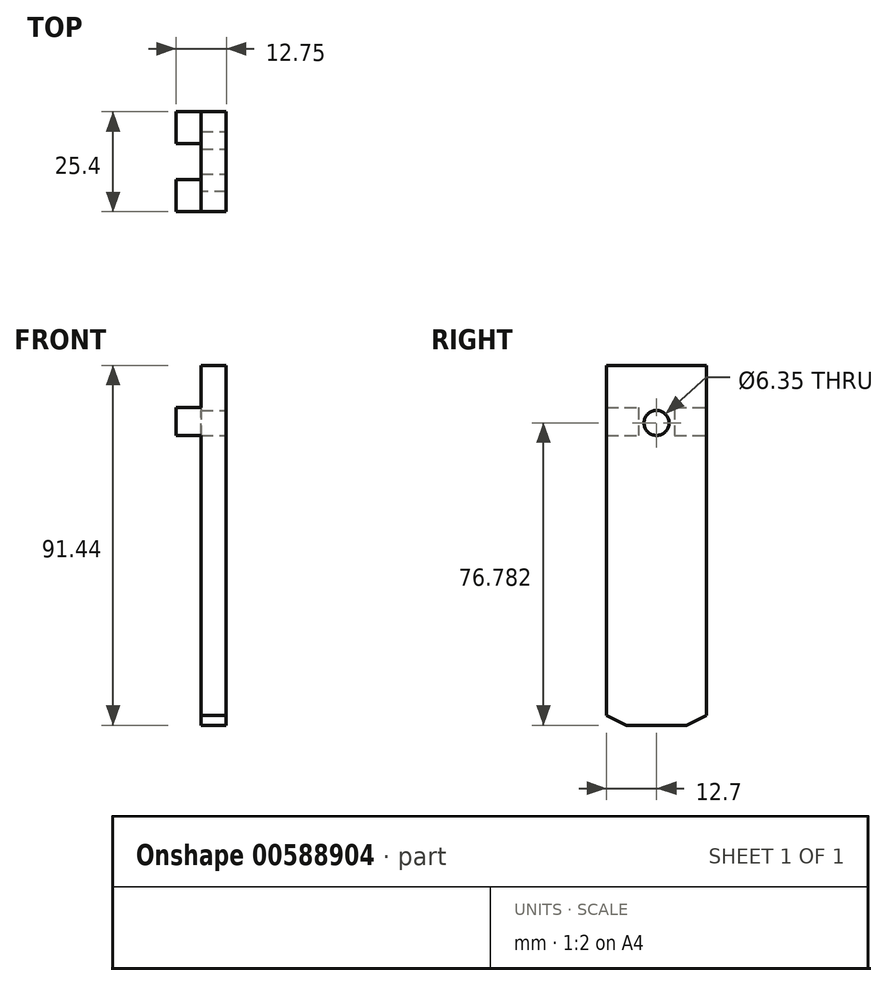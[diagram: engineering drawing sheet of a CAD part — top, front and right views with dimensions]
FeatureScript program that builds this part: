
annotation { "Feature Type Name" : "Feature", "Feature Type Description" : "" }
export const myFeature = defineFeature(function(context is Context, id is Id, definition is map)
    precondition{}
    {
        {
            var Q0;
            Q0=qCreatedBy(makeId("Front.planeOp"),FACE);
            var sketch = newSketch(context, id + "F0", { "sketchPlane" : qUnion([Q0])});
            skLineSegment(sketch, "E0.right", {"start": v(75.76, 44.96) * mm, "end": v(75.76, 34.21) * mm});
            skLineSegment(sketch, "E1", {"start": v(75.76, 44.96) * mm, "end": v(82.1, 44.96) * mm});
            skLineSegment(sketch, "E2", {"start": v(82.1, 44.96) * mm, "end": v(82.1, -46.48) * mm});
            skLineSegment(sketch, "E3.bottom", {"start": v(75.76, 34.21) * mm, "end": v(69.36, 34.21) * mm});
            skLineSegment(sketch, "E3.top", {"start": v(75.76, 27.1) * mm, "end": v(69.36, 27.1) * mm});
            skLineSegment(sketch, "E3.right", {"start": v(69.36, 34.21) * mm, "end": v(69.36, 27.1) * mm});
            skLineSegment(sketch, "E4.trimOffspring", {"start": v(75.76, 27.1) * mm, "end": v(75.76, -46.48) * mm});
            skLineSegment(sketch, "E5", {"start": v(82.1, -46.48) * mm, "end": v(75.76, -46.48) * mm});
            skSolve(sketch);
        }
        {
            var Q0;
            Q0=makeQuery(id+"F0.imprint","IMPRINT",FACE,{"disambiguationData":[TD([[makeQuery(id+"F0.imprint","IMPRINT",EDGE,{"derivedFrom":sQuery(id+"F0.wireOp",EDGE,"E0.right")}),1.0]])]});
            extrude(context, id + "F1", {"entities" : qUnion([Q0]), "depth" : 25.4 * mm, "offsetDistance" : 25.4 * mm});
        }
        {
            var Q0;
            Q0=makeQuery(id+"F1.opExtrude","SWEPT_FACE",FACE,{"disambiguationData":[OSD([sQuery(id+"F0.wireOp",EDGE,"E2")])]});
            var sketch = newSketch(context, id + "F2", { "sketchPlane" : qUnion([Q0])});
            skLineSegment(sketch, "E6", {"start": v(-12.7, 44.96) * mm, "end": v(-12.7, 30.3) * mm});
            skCircle(sketch, "E7", {"center": v(-12.7, 30.3) * mm, "radius": 3.18 * mm});
            skSolve(sketch);
        }
        {
            var Q0;
            Q0=makeQuery(id+"F1.opExtrude","SWEPT_FACE",FACE,{"disambiguationData":[OSD([sQuery(id+"F0.wireOp",EDGE,"E3.right")])]});
            var sketch = newSketch(context, id + "F3", { "sketchPlane" : qUnion([Q0])});
            skLineSegment(sketch, "E8.0", {"start": v(17.27, 34.21) * mm, "end": v(17.27, 27.1) * mm});
            skLineSegment(sketch, "E9.0", {"start": v(8.13, 34.21) * mm, "end": v(8.13, 27.1) * mm});
            skSolve(sketch);
        }
        {
            var Q0;
            {var subQ0=sQuery(id+"F3.wireOp",EDGE,"E8.0");Q0=makeQuery(id+"F3.imprint","IMPRINT",FACE,{"disambiguationData":[TD([[makeQuery(id+"F3.imprint","IMPRINT",EDGE,{"derivedFrom":subQ0}),-1.0]])]});}
            var Q1;
            Q1=makeQuery(id+"F1.opExtrude","SWEPT_FACE",FACE,{"disambiguationData":[OSD([sQuery(id+"F0.wireOp",EDGE,"E0.right")])]});
            extrude(context, id + "F4", {"entities" : qUnion([Q0]), "operationType" : NewBodyOperationType.REMOVE, "endBound" : BoundingType.UP_TO_SURFACE, "oppositeDirection" : true, "depth" : 25.4 * mm, "endBoundEntityFace" : qUnion([Q1]), "offsetDistance" : 25.4 * mm});
        }
        {
            var Q0;
            Q0=makeQuery(id+"F2.imprint","IMPRINT",FACE,{"disambiguationData":[TD([[makeQuery(id+"F2.imprint","IMPRINT",EDGE,{"derivedFrom":sQuery(id+"F2.wireOp",EDGE,"E7")}),1.0]])]});
            extrude(context, id + "F5", {"entities" : qUnion([Q0]), "operationType" : NewBodyOperationType.REMOVE, "endBound" : BoundingType.UP_TO_NEXT, "oppositeDirection" : true, "depth" : 25.4 * mm, "offsetDistance" : 25.4 * mm});
        }
        {
            var Q0;
            Q0=makeQuery(id+"F1.opExtrude","CAP_EDGE",EDGE,{"disambiguationData":[OSD([sQuery(id+"F0.wireOp",EDGE,"E5")])],"isStart":false});
            var Q1;
            Q1=makeQuery(id+"F1.opExtrude","CAP_EDGE",EDGE,{"disambiguationData":[OSD([sQuery(id+"F0.wireOp",EDGE,"E5")])],"isStart":true});
            chamfer(context, id + "F6", {"entities" : qUnion([Q0, Q1]), "chamferType" : ChamferType.TWO_OFFSETS, "width1" : 5.08 * mm, "oppositeDirection" : false, "width2" : 2.54 * mm, "tangentPropagation" : true});
        }
    });
